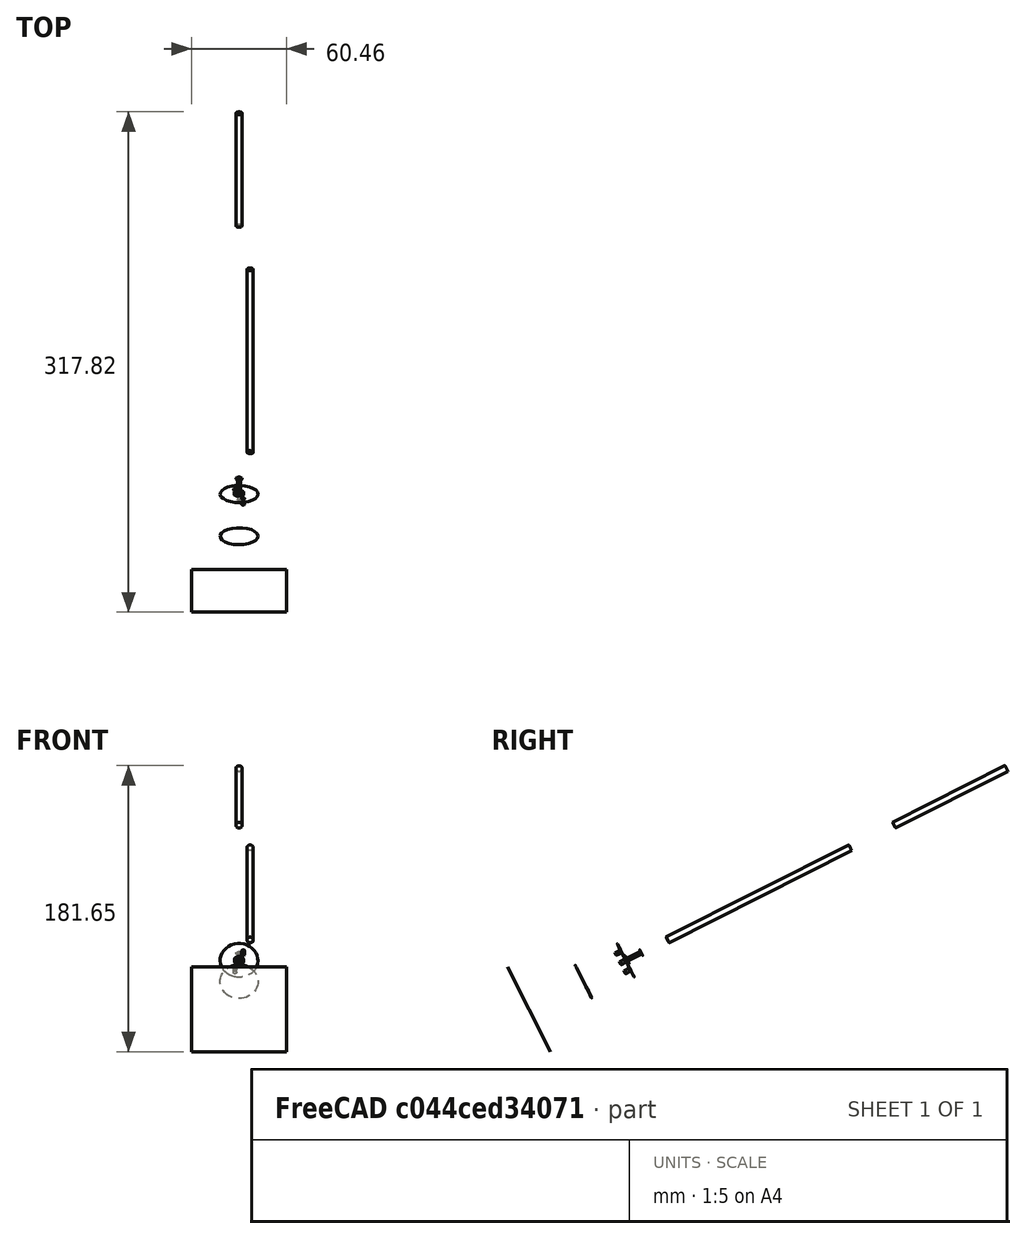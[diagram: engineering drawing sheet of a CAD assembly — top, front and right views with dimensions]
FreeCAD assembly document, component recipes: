
FREECAD ASSEMBLY — COMPONENT RECIPES ("sailface_prop_motor_assembly")

This assembly document has 4 components, labeled P0..P3 below (a component is one placed body or linked part). 2 of them carry a construction recipe — the FreeCAD feature program that regenerates the part from scratch, quoted from this document or its linked companion documents; the rest are supplied as boundary geometry only. No exploded tour is included for this assembly.
COMPONENT P0 — geometry summary ("PropShaftSleeve"; no construction recipe available for this part):
  bounding box: 74.1 x 41.4 x 6.0 mm
  tessellated surface: 932 triangles
  volume: 1257 mm^3 (7% of its bounding box)
COMPONENT P1 — recipe-attached ("PropAndShaft", a linked part whose construction recipe lives in a companion FreeCAD document of the same project; that document's serialized recipe follows).
Construction recipe (the companion document, serialized — sketch geometry with constraints, then the solid features built on it; lengths are millimeters unless a unit is written):

FCSTD DOCUMENT  (FreeCAD 0.19R24366 (Git))
Label: Prop_uxcell_prop_shaft
License: All rights reserved
LicenseURL: http://en.wikipedia.org/wiki/All_rights_reserved
objects: Sketcher::SketchObject×6, Part::Extrusion×3, App::Part×3, PartDesign::Pocket×2, Mesh::Feature×1, PartDesign::Pad×1, PartDesign::Body×1
note: 16 computed .brp shape members not serialized (recipe doc carries the construction recipe); baked Part::Feature solids carry a one-line shape summary decoded from their .brp

FEATURE [Mesh::Feature] driveshaft
FEATURE [Sketcher::SketchObject] Sketch
  FullyConstrained = true
  sketch-geometry (2):
    g0: Circle CenterX=0 CenterY=0 CenterZ=0 NormalX=0 NormalY=0 NormalZ=1 AngleXU=0 Radius=3
    g1: Circle CenterX=0 CenterY=0 CenterZ=0 NormalX=0 NormalY=0 NormalZ=1 AngleXU=0 Radius=2
  constraints (4):
    c: Coincident(g0,g1)
    c: Coincident(g0,g-1)
    c: Diameter(g1) = 4
    c: Diameter(g0) = 6
FEATURE [Part::Extrusion] Extrude  label="PropShaftSleeve001"
  Base = -> Sketch
  Dir = (0,0,1)
  DirMode = 0
  FaceMakerClass = Part::FaceMakerBullseye
  LengthFwd = 80
  LengthRev = 0
  Solid = true
  Symmetric = false
FEATURE [App::Part] Part  label="PropShaftSleeve"
  Group = -> [Sketch,Extrude]
  Origin = -> Origin
FEATURE [Sketcher::SketchObject] Sketch001
  FullyConstrained = false
  sketch-geometry (8):
    g0: Circle CenterX=0 CenterY=0 CenterZ=0 NormalX=0 NormalY=0 NormalZ=1 AngleXU=0 Radius=3
    g1: LineSegment StartX=-2.96858 StartY=0.433018 StartZ=0 EndX=-0.480038 EndY=17.4934 EndZ=0
    g2: LineSegment StartX=2.15757 StartY=2.08444 StartZ=0 EndX=-0.480038 EndY=17.4934 EndZ=0
    g3: LineSegment StartX=-2.96858 StartY=0.433018 StartZ=0 EndX=-16.5261 EndY=-5.75668 EndZ=0
    g4: LineSegment StartX=-16.5261 StartY=-5.75668 StartZ=0 EndX=-0.463294 EndY=-3.11641 EndZ=0
    g5: LineSegment StartX=-0.463294 StartY=-3.11641 StartZ=0 EndX=14.1368 EndY=-10.3151 EndZ=0
    g6: LineSegment StartX=14.1368 StartY=-10.3151 StartZ=0 EndX=2.15757 EndY=2.08444 EndZ=0
    g7: Circle CenterX=0 CenterY=0 CenterZ=0 NormalX=0 NormalY=0 NormalZ=1 AngleXU=0 Radius=17.5
  constraints (19):
    c: Coincident(g0,g-1)
    c: Diameter(g0) = 6
    c: PointOnObject(g1,g0)
    c: PointOnObject(g2,g0)
    c: Coincident(g2,g1)
    c: Coincident(g4,g3)
    c: Coincident(g4,g5)
    c: Tangent(g5,g0)
    c: Tangent(g4,g0)
    c: Coincident(g3,g1)
    c: Coincident(g2,g6)
    c: Coincident(g7,g0)
    c: PointOnObject(g5,g7)
    c: PointOnObject(g3,g7)
    c: PointOnObject(g1,g7)
    c: Coincident(g6,g5)
    c: Diameter(g7) = 35
    c: Tangent(g0,g1,g1) = 1.5708
    c: Tangent(g6,g0,g2) = -1.5708
FEATURE [Part::Extrusion] Extrude001  label="PropMock"
  Base = -> Sketch001
  Dir = (0,0,-1)
  DirMode = 0
  FaceMakerClass = Part::FaceMakerBullseye
  LengthFwd = 3
  LengthRev = 0
  Solid = true
  Symmetric = false
FEATURE [Sketcher::SketchObject] Sketch002
  FullyConstrained = true
  sketch-geometry (1):
    g0: Circle CenterX=0 CenterY=0 CenterZ=0 NormalX=0 NormalY=0 NormalZ=1 AngleXU=0 Radius=2
  constraints (2):
    c: Coincident(g0,g-1)
    c: Diameter(g0) = 4
FEATURE [Part::Extrusion] Extrude002  label="PropShaft"
  Base = -> Sketch002
  Dir = (0,0,-1)
  DirMode = 0
  FaceMakerClass = Part::FaceMakerBullseye
  LengthFwd = 130
  LengthRev = 0
  Solid = true
  Symmetric = false
FEATURE [App::Part] Part001  label="PropAndShaft"
  Group = -> [Sketch001,Extrude001,Sketch002,Extrude002]
  Origin = -> Origin001
FEATURE [Sketcher::SketchObject] Sketch003
  FullyConstrained = true
  MapMode = 5
  Support = -> [XY_Plane003]
  sketch-geometry (1):
    g0: Circle CenterX=0 CenterY=0 CenterZ=0 NormalX=0 NormalY=0 NormalZ=1 AngleXU=0 Radius=3
  constraints (2):
    c: Coincident(g0,g-1)
    c: Diameter(g0) = 6
FEATURE [PartDesign::Pad] Pad
  Direction = (1,1,1)
  Length = 20
  Length2 = 100
  Profile = -> Sketch003
  Type = 0
FEATURE [Sketcher::SketchObject] Sketch004
  FullyConstrained = true
  MapMode = 5
  Placement = pos=(0,0,20) rot=(0,0,1;0rad)
  Support = -> [Pad]
  sketch-geometry (1):
    g0: Circle CenterX=0 CenterY=0 CenterZ=0 NormalX=0 NormalY=0 NormalZ=1 AngleXU=0 Radius=2
  constraints (2):
    c: Coincident(g0,g-1)
    c: Diameter(g0) = 4
FEATURE [PartDesign::Pocket] Pocket
  BaseFeature = -> Pad
  Length = 5
  Length2 = 100
  Profile = -> Sketch004
  Type = 0
FEATURE [Sketcher::SketchObject] Sketch005
  FullyConstrained = true
  MapMode = 5
  Placement = pos=(0,0,0) rot=(1,0,0;3.14159rad)
  Support = -> [Pocket]
  sketch-geometry (1):
    g0: Circle CenterX=0 CenterY=0 CenterZ=0 NormalX=0 NormalY=0 NormalZ=1 AngleXU=0 Radius=1
  constraints (2):
    c: Coincident(g0,g-1)
    c: Diameter(g0) = 2
FEATURE [PartDesign::Pocket] Pocket001
  BaseFeature = -> Pocket
  Length = 5
  Length2 = 100
  Profile = -> Sketch005
  Type = 0
FEATURE [PartDesign::Body] Body
  Group = -> [Sketch003,Pad,Sketch004,Pocket,Sketch005,Pocket001]
  Origin = -> Origin003
  Tip = -> Pocket001
FEATURE [App::Part] Part002  label="ShaftConnectorTemp"
  Group = -> [Body]
  Origin = -> Origin002
COMPONENT P2 — geometry summary ("MotorPart"; no construction recipe available for this part):
  bounding box: 42.5 x 34.9 x 24.0 mm
  tessellated surface: 1,652 triangles
  volume: 13606 mm^3 (38% of its bounding box)
COMPONENT P3 — same part as P1; its construction recipe is shown at P1.
PROVENANCE & LICENSES
A FreeCAD (.FCStd) document from a public repository crawl; recipes are the document's own serialized feature recipes (and, for linked parts, companion documents' recipes).
License: as declared in the source repository (recorded in the dataset sidecar).
